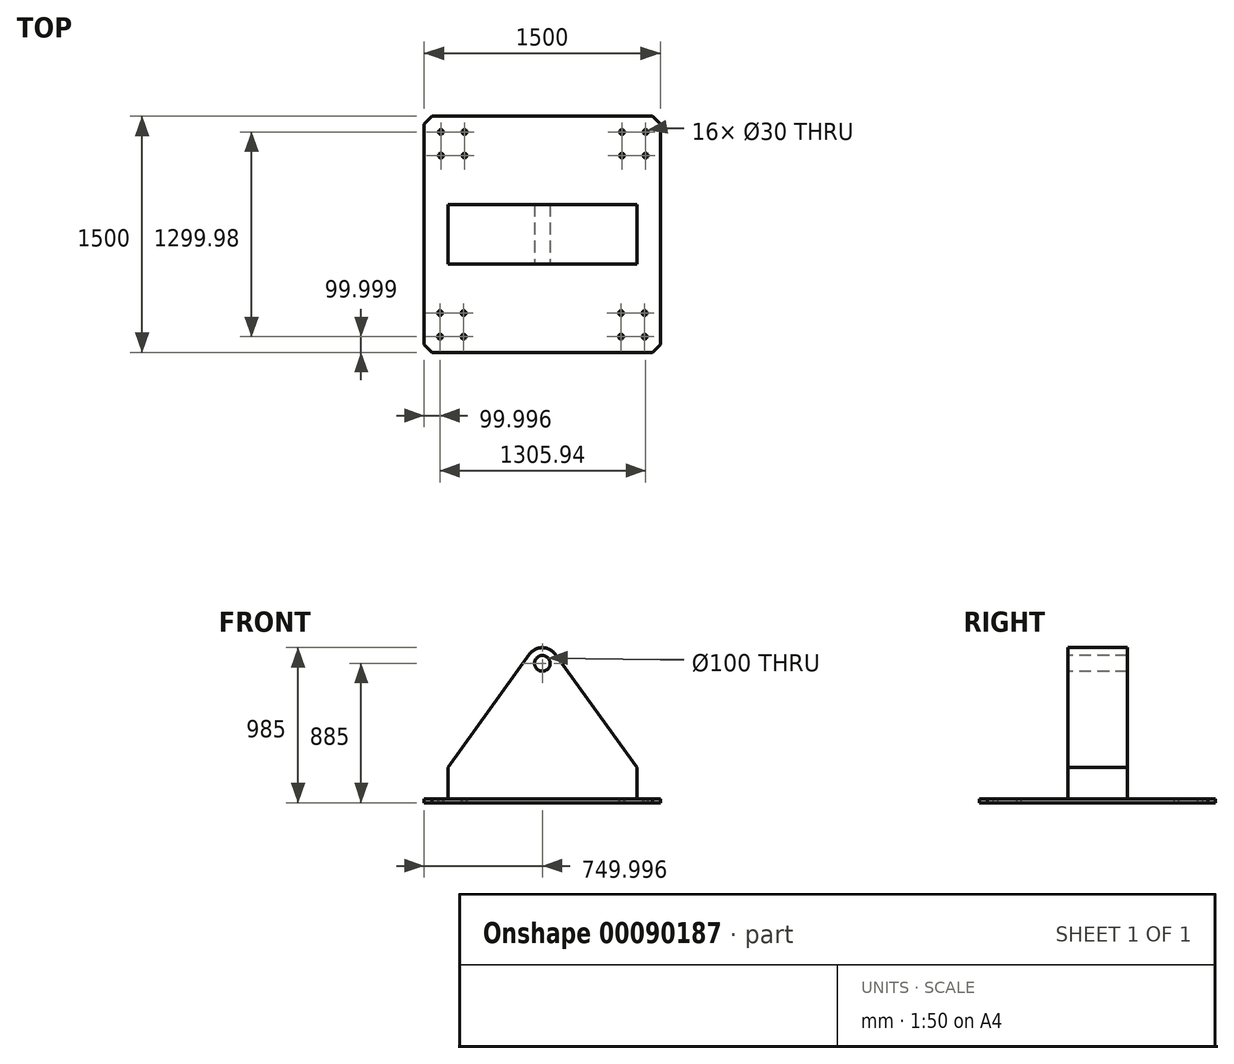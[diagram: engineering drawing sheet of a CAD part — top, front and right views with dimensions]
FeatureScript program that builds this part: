
annotation { "Feature Type Name" : "Feature", "Feature Type Description" : "" }
export const myFeature = defineFeature(function(context is Context, id is Id, definition is map)
    precondition{}
    {
        {
            var Q0;
            Q0=qCreatedBy(makeId("Top.planeOp"),FACE);
            var sketch = newSketch(context, id + "F0", { "sketchPlane" : qUnion([Q0])});
            skLineSegment(sketch, "E0.bottom", {"start": v(-1388.34, 1391.2) * mm, "end": v(111.66, 1391.2) * mm});
            skLineSegment(sketch, "E0.top", {"start": v(-1388.34, -108.8) * mm, "end": v(111.66, -108.8) * mm});
            skLineSegment(sketch, "E0.left", {"start": v(-1388.34, 1391.2) * mm, "end": v(-1388.34, -108.8) * mm});
            skLineSegment(sketch, "E0.right", {"start": v(111.66, 1391.2) * mm, "end": v(111.66, -108.8) * mm});
            skSolve(sketch);
        }
        {
            var Q0;
            Q0=makeQuery(id+"F0.imprint","IMPRINT",FACE,{"disambiguationData":[TD([[makeQuery(id+"F0.imprint","IMPRINT",EDGE,{"derivedFrom":sQuery(id+"F0.wireOp",EDGE,"E0.bottom")}),-1.0]])]});
            extrude(context, id + "F1", {"entities" : qUnion([Q0]), "depth" : 25 * mm});
        }
        {
            var Q0;
            Q0=makeQuery(id+"F1.opExtrude","SWEPT_EDGE",EDGE,{"disambiguationData":[OSD([sQuery(id+"F0.wireOp",EDGE,"E0.top"),sQuery(id+"F0.wireOp",EDGE,"E0.left")])]});
            var Q1;
            Q1=makeQuery(id+"F1.opExtrude","SWEPT_EDGE",EDGE,{"disambiguationData":[OSD([sQuery(id+"F0.wireOp",EDGE,"E0.top"),sQuery(id+"F0.wireOp",EDGE,"E0.right")])]});
            var Q2;
            Q2=makeQuery(id+"F1.opExtrude","SWEPT_EDGE",EDGE,{"disambiguationData":[OSD([sQuery(id+"F0.wireOp",EDGE,"E0.bottom"),sQuery(id+"F0.wireOp",EDGE,"E0.right")])]});
            var Q3;
            Q3=makeQuery(id+"F1.opExtrude","SWEPT_EDGE",EDGE,{"disambiguationData":[OSD([sQuery(id+"F0.wireOp",EDGE,"E0.bottom"),sQuery(id+"F0.wireOp",EDGE,"E0.left")])]});
            chamfer(context, id + "F2", {"entities" : qUnion([Q0, Q1, Q2, Q3]), "width" : 50 * mm, "tangentPropagation" : true});
        }
        {
            var Q0;
            Q0=makeQuery(id+"F1.opExtrude","CAP_FACE",FACE,{"disambiguationData":[OSD([sQuery(id+"F0.wireOp",EDGE,"E0.bottom"),sQuery(id+"F0.wireOp",EDGE,"E0.top"),sQuery(id+"F0.wireOp",EDGE,"E0.left"),sQuery(id+"F0.wireOp",EDGE,"E0.right")])],"isStart":false});
            var sketch = newSketch(context, id + "F3", { "sketchPlane" : qUnion([Q0])});
            skLineSegment(sketch, "E1.bottom", {"start": v(-1238.34, 830.2) * mm, "end": v(-38.34, 830.2) * mm});
            skLineSegment(sketch, "E1.top", {"start": v(-1238.34, 452.2) * mm, "end": v(-38.34, 452.2) * mm});
            skLineSegment(sketch, "E1.left", {"start": v(-1238.34, 830.2) * mm, "end": v(-1238.34, 452.2) * mm});
            skLineSegment(sketch, "E1.right", {"start": v(-38.34, 830.2) * mm, "end": v(-38.34, 452.2) * mm});
            skSolve(sketch);
        }
        {
            var Q0;
            Q0=makeQuery(id+"F3.imprint","IMPRINT",FACE,{"disambiguationData":[TD([[makeQuery(id+"F3.imprint","IMPRINT",EDGE,{"derivedFrom":sQuery(id+"F3.wireOp",EDGE,"E1.bottom")}),-1.0]])]});
            extrude(context, id + "F4", {"entities" : qUnion([Q0]), "operationType" : NewBodyOperationType.ADD, "depth" : 960 * mm});
        }
        {
            var Q0;
            Q0=makeQuery(id+"F4.opExtrude","SWEPT_FACE",FACE,{"disambiguationData":[OSD([sQuery(id+"F3.wireOp",EDGE,"E1.top")])]});
            var sketch = newSketch(context, id + "F5", { "sketchPlane" : qUnion([Q0])});
            skPoint(sketch, "E2", {"position": v(-638.34, 885) * mm});
            skSolve(sketch);
        }
        {
            var Q0;
            Q0=sQuery(id+"F5.wireOp",VERTEX,"E2");
            var Q1;
            Q1=makeQuery(id+"F1.opExtrude","SWEPT_BODY",BODY,{"disambiguationData":[OSD([sQuery(id+"F0.wireOp",EDGE,"E0.bottom"),sQuery(id+"F0.wireOp",EDGE,"E0.top"),sQuery(id+"F0.wireOp",EDGE,"E0.left"),sQuery(id+"F0.wireOp",EDGE,"E0.right")])]});
            hole(context, id + "F6", {"style" : HoleStyle.SIMPLE, "endStyle" : HoleEndStyle.THROUGH, "holeDiameter" : 100 * mm, "locations" : qUnion([Q0]), "scope" : qUnion([Q1]), "isTappedThrough" : true});
        }
        {
            var Q0;
            Q0=makeQuery(id+"F4.opExtrude","SWEPT_FACE",FACE,{"disambiguationData":[OSD([sQuery(id+"F3.wireOp",EDGE,"E1.top")])]});
            var sketch = newSketch(context, id + "F7", { "sketchPlane" : qUnion([Q0])});
            skLineSegment(sketch, "E3", {"start": v(-1238.34, 225) * mm, "end": v(-719.41, 943.55) * mm});
            skLineSegment(sketch, "E4", {"start": v(-38.34, 225) * mm, "end": v(-557.28, 943.55) * mm});
            skArc(sketch, "E5", {"start": v(-719.41, 943.55) * mm, "mid": v(-638.34, 985) * mm, "end": v(-557.28, 943.55) * mm});
            skLineSegment(sketch, "E6", {"start": v(-1238.34, 225) * mm, "end": v(-1238.34, 985) * mm});
            skLineSegment(sketch, "E7", {"start": v(-1238.34, 985) * mm, "end": v(-638.34, 985) * mm});
            skLineSegment(sketch, "E8", {"start": v(-638.34, 985) * mm, "end": v(-38.34, 985) * mm});
            skLineSegment(sketch, "E9", {"start": v(-38.34, 985) * mm, "end": v(-38.34, 225) * mm});
            skSolve(sketch);
        }
        {
            var Q0;
            {var subQ0=sQuery(id+"F7.wireOp",EDGE,"E3");Q0=makeQuery(id+"F7.imprint","IMPRINT",FACE,{"disambiguationData":[TD([[makeQuery(id+"F7.imprint","IMPRINT",EDGE,{"derivedFrom":subQ0}),1.0]])]});}
            var Q1;
            {var subQ0=sQuery(id+"F7.wireOp",EDGE,"E4");Q1=makeQuery(id+"F7.imprint","IMPRINT",FACE,{"disambiguationData":[TD([[makeQuery(id+"F7.imprint","IMPRINT",EDGE,{"derivedFrom":subQ0}),-1.0]])]});}
            extrude(context, id + "F8", {"entities" : qUnion([Q0, Q1]), "operationType" : NewBodyOperationType.REMOVE, "oppositeDirection" : true, "depth" : 532.3 * mm});
        }
        {
            var Q0;
            Q0=makeQuery(id+"F1.opExtrude","CAP_FACE",FACE,{"disambiguationData":[OSD([sQuery(id+"F0.wireOp",EDGE,"E0.bottom"),sQuery(id+"F0.wireOp",EDGE,"E0.top"),sQuery(id+"F0.wireOp",EDGE,"E0.left"),sQuery(id+"F0.wireOp",EDGE,"E0.right")])],"isStart":true});
            var sketch = newSketch(context, id + "F9", { "sketchPlane" : qUnion([Q0])});
            skPoint(sketch, "E10", {"position": v(-1288.34, 8.8) * mm});
            skPoint(sketch, "E11", {"position": v(-1138.34, 8.8) * mm});
            skPoint(sketch, "E12", {"position": v(-1138.34, -141.2) * mm});
            skPoint(sketch, "E13", {"position": v(-1288.34, -141.2) * mm});
            skPoint(sketch, "E14.0.1.0", {"position": v(-1282.4, -1141.2) * mm});
            skPoint(sketch, "E14.0.1.1", {"position": v(-1282.4, -1291.2) * mm});
            skPoint(sketch, "E14.0.1.2", {"position": v(-1132.4, -1291.2) * mm});
            skPoint(sketch, "E14.0.1.3", {"position": v(-1132.4, -1141.2) * mm});
            skPoint(sketch, "E14.1.0.0", {"position": v(-138.34, 8.8) * mm});
            skPoint(sketch, "E14.1.0.1", {"position": v(-138.34, -141.2) * mm});
            skPoint(sketch, "E14.1.0.2", {"position": v(11.66, -141.2) * mm});
            skPoint(sketch, "E14.1.0.3", {"position": v(11.66, 8.8) * mm});
            skPoint(sketch, "E14.1.1.0", {"position": v(-132.4, -1141.2) * mm});
            skPoint(sketch, "E14.1.1.1", {"position": v(-132.4, -1291.2) * mm});
            skPoint(sketch, "E14.1.1.2", {"position": v(17.6, -1291.2) * mm});
            skPoint(sketch, "E14.1.1.3", {"position": v(17.6, -1141.2) * mm});
            skLineSegment(sketch, "E14.direction1", {"start": v(-1288.34, 8.8) * mm, "end": v(-138.34, 8.8) * mm, "construction": true});
            skLineSegment(sketch, "E14.direction2", {"start": v(-1288.34, 8.8) * mm, "end": v(-1282.4, -1141.2) * mm, "construction": true});
            skSolve(sketch);
        }
        {
            var Q0;
            Q0=sQuery(id+"F9.wireOp",VERTEX,"E14.0.1.1");
            var Q1;
            Q1=sQuery(id+"F9.wireOp",VERTEX,"E14.0.1.2");
            var Q2;
            Q2=sQuery(id+"F9.wireOp",VERTEX,"E14.0.1.3");
            var Q3;
            Q3=sQuery(id+"F9.wireOp",VERTEX,"E14.0.1.0");
            var Q4;
            Q4=sQuery(id+"F9.wireOp",VERTEX,"E13");
            var Q5;
            Q5=sQuery(id+"F9.wireOp",VERTEX,"E12");
            var Q6;
            Q6=sQuery(id+"F9.wireOp",VERTEX,"E11");
            var Q7;
            Q7=sQuery(id+"F9.wireOp",VERTEX,"E10");
            var Q8;
            Q8=sQuery(id+"F9.wireOp",VERTEX,"E14.1.0.0");
            var Q9;
            Q9=sQuery(id+"F9.wireOp",VERTEX,"E14.1.0.3");
            var Q10;
            Q10=sQuery(id+"F9.wireOp",VERTEX,"E14.1.0.2");
            var Q11;
            Q11=sQuery(id+"F9.wireOp",VERTEX,"E14.1.0.1");
            var Q12;
            Q12=sQuery(id+"F9.wireOp",VERTEX,"E14.1.1.0");
            var Q13;
            Q13=sQuery(id+"F9.wireOp",VERTEX,"E14.1.1.3");
            var Q14;
            Q14=sQuery(id+"F9.wireOp",VERTEX,"E14.1.1.2");
            var Q15;
            Q15=sQuery(id+"F9.wireOp",VERTEX,"E14.1.1.1");
            var Q16;
            Q16=makeQuery(id+"F1.opExtrude","SWEPT_BODY",BODY,{"disambiguationData":[OSD([sQuery(id+"F0.wireOp",EDGE,"E0.bottom"),sQuery(id+"F0.wireOp",EDGE,"E0.top"),sQuery(id+"F0.wireOp",EDGE,"E0.left"),sQuery(id+"F0.wireOp",EDGE,"E0.right")])]});
            hole(context, id + "F10", {"style" : HoleStyle.SIMPLE, "endStyle" : HoleEndStyle.THROUGH, "holeDiameter" : 30 * mm, "locations" : qUnion([Q0, Q1, Q2, Q3, Q4, Q5, Q6, Q7, Q8, Q9, Q10, Q11, Q12, Q13, Q14, Q15]), "scope" : qUnion([Q16]), "isTappedThrough" : true});
        }
    });
